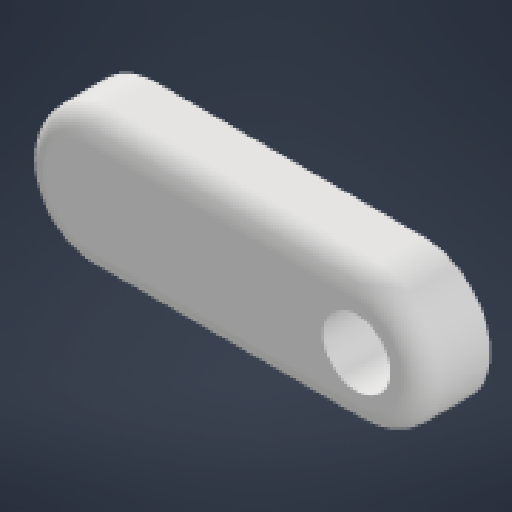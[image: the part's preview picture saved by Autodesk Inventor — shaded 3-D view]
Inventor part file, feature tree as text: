
AUTODESK INVENTOR PART (.ipt)
format: ipt  version: 2024.3 (Build 283343000, 343)  size: 140,800 bytes
history: native  units: in
note: dims shown in document units (in); Inventor stores cm internally (conversion verified against a paired STEP export)
features: extrude x1, fillet x1, sketch x1
ambient origin geometry x8: Origin, YZ Plane, XZ Plane, XY Plane, X Axis, Y Axis, Z Axis, Center Point
bodies: Solid1 (feature_tree)
feature tree (3):
  extrude  "Extrusion1"  Depth=0.75in
  fillet  "Fillet1"  Radius=0.375in
  sketch  "Sketch1"  dims[d0=0.1875in d2=0.75in d3=0.375in d4=0.1875in d5=0.0in d6=0.0625in]
